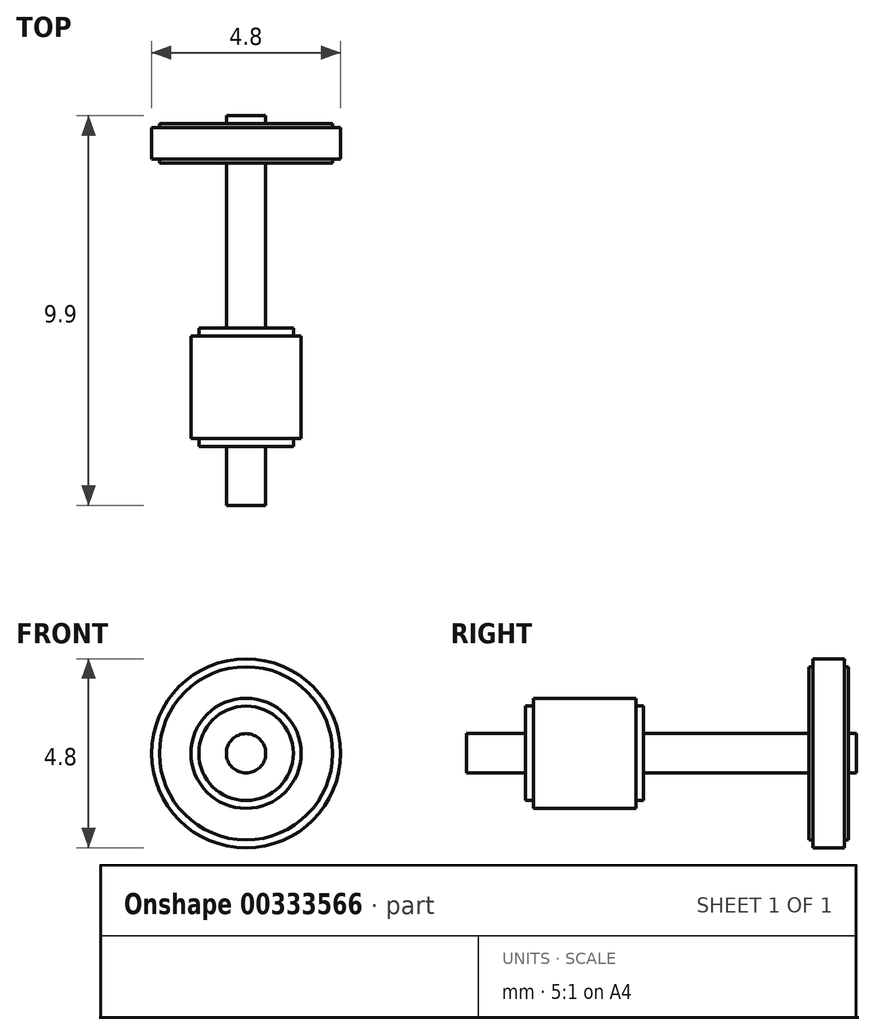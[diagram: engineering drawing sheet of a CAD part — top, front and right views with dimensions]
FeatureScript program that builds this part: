
annotation { "Feature Type Name" : "Feature", "Feature Type Description" : "" }
export const myFeature = defineFeature(function(context is Context, id is Id, definition is map)
    precondition{}
    {
        {
            var Q0;
            Q0=qCreatedBy(makeId("Right.planeOp"),FACE);
            var sketch = newSketch(context, id + "F0", { "sketchPlane" : qUnion([Q0])});
            skLineSegment(sketch, "E0", {"start": v(-1.5, 0) * mm, "end": v(-1.5, 0.5) * mm});
            skLineSegment(sketch, "E1", {"start": v(-1.5, 0.5) * mm, "end": v(0, 0.5) * mm});
            skLineSegment(sketch, "E2", {"start": v(0, 0.5) * mm, "end": v(0, 1.4) * mm});
            skLineSegment(sketch, "E3", {"start": v(0, 1.4) * mm, "end": v(3, 1.4) * mm});
            skLineSegment(sketch, "E4", {"start": v(3, 1.4) * mm, "end": v(3, 0.5) * mm});
            skLineSegment(sketch, "E5", {"start": v(3, 0.5) * mm, "end": v(7.2, 0.5) * mm});
            skLineSegment(sketch, "E6", {"start": v(7.2, 0.5) * mm, "end": v(7.2, 2.4) * mm});
            skLineSegment(sketch, "E7", {"start": v(7.2, 2.4) * mm, "end": v(8.2, 2.4) * mm});
            skLineSegment(sketch, "E8", {"start": v(8.2, 2.4) * mm, "end": v(8.2, 0.5) * mm});
            skLineSegment(sketch, "E9", {"start": v(8.2, 0.5) * mm, "end": v(8.4, 0.5) * mm});
            skLineSegment(sketch, "E10", {"start": v(8.4, 0.5) * mm, "end": v(8.4, 0) * mm});
            skLineSegment(sketch, "E11", {"start": v(8.4, 0) * mm, "end": v(-1.5, 0) * mm});
            skSolve(sketch);
        }
        {
            var Q0;
            Q0=qSketchRegion(id+"F0",true);
            var Q1;
            Q1=sQuery(id+"F0.wireOp",EDGE,"E11");
            revolve(context, id + "F1", {"entities" : qUnion([Q0]), "axis" : qUnion([Q1]), "revolveType" : RevolveType.FULL});
        }
        {
            var Q0;
            Q0=qCreatedBy(makeId("Right.planeOp"),FACE);
            var sketch = newSketch(context, id + "F2", { "sketchPlane" : qUnion([Q0])});
            skLineSegment(sketch, "E12.0", {"start": v(0, 1.4) * mm, "end": v(3, 1.4) * mm});
            skLineSegment(sketch, "E13.0", {"start": v(0, 0.5) * mm, "end": v(0, 1.4) * mm});
            skLineSegment(sketch, "E14.0", {"start": v(3, 1.4) * mm, "end": v(3, 0.5) * mm});
            skLineSegment(sketch, "E15.bottom", {"start": v(0, 1.4) * mm, "end": v(0.2, 1.4) * mm});
            skLineSegment(sketch, "E15.top", {"start": v(0, 1.2) * mm, "end": v(0.2, 1.2) * mm});
            skLineSegment(sketch, "E15.left", {"start": v(0, 1.4) * mm, "end": v(0, 1.2) * mm});
            skLineSegment(sketch, "E15.right", {"start": v(0.2, 1.4) * mm, "end": v(0.2, 1.2) * mm});
            skLineSegment(sketch, "E16.bottom", {"start": v(3, 1.4) * mm, "end": v(2.8, 1.4) * mm});
            skLineSegment(sketch, "E16.top", {"start": v(3, 1.2) * mm, "end": v(2.8, 1.2) * mm});
            skLineSegment(sketch, "E16.left", {"start": v(3, 1.4) * mm, "end": v(3, 1.2) * mm});
            skLineSegment(sketch, "E16.right", {"start": v(2.8, 1.4) * mm, "end": v(2.8, 1.2) * mm});
            skSolve(sketch);
        }
        {
            var Q0;
            Q0 = qSketchRegion(id + "F2", true);
            var Q1;
            Q1=sQuery(id+"F0.wireOp",EDGE,"E11");
            revolve(context, id + "F3", {"operationType" : NewBodyOperationType.REMOVE, "surfaceOperationType" : NewSurfaceOperationType.NEW, "entities" : qUnion([Q0]), "axis" : qUnion([Q1]), "revolveType" : RevolveType.FULL, "oppositeDirection" : true});
        }
        {
            var Q0;
            Q0=qCreatedBy(makeId("Right.planeOp"),FACE);
            var sketch = newSketch(context, id + "F4", { "sketchPlane" : qUnion([Q0])});
            skLineSegment(sketch, "E17.0", {"start": v(7.2, 2.4) * mm, "end": v(8.2, 2.4) * mm});
            skLineSegment(sketch, "E18", {"start": v(8.2, -2.4) * mm, "end": v(7.2, -2.4) * mm});
            skLineSegment(sketch, "E19.0", {"start": v(8.2, 2.4) * mm, "end": v(8.2, 0.5) * mm});
            skLineSegment(sketch, "E20.bottom", {"start": v(8.2, 2.4) * mm, "end": v(8.1, 2.4) * mm});
            skLineSegment(sketch, "E20.top", {"start": v(8.2, 2.2) * mm, "end": v(8.1, 2.2) * mm});
            skLineSegment(sketch, "E20.left", {"start": v(8.2, 2.4) * mm, "end": v(8.2, 2.2) * mm});
            skLineSegment(sketch, "E20.right", {"start": v(8.1, 2.4) * mm, "end": v(8.1, 2.2) * mm});
            skLineSegment(sketch, "E21.bottom", {"start": v(7.2, 2.4) * mm, "end": v(7.3, 2.4) * mm});
            skLineSegment(sketch, "E21.top", {"start": v(7.2, 2.2) * mm, "end": v(7.3, 2.2) * mm});
            skLineSegment(sketch, "E21.left", {"start": v(7.2, 2.4) * mm, "end": v(7.2, 2.2) * mm});
            skLineSegment(sketch, "E21.right", {"start": v(7.3, 2.4) * mm, "end": v(7.3, 2.2) * mm});
            skSolve(sketch);
        }
        {
            var Q0;
            Q0 = qSketchRegion(id + "F4", true);
            var Q1;
            Q1=sQuery(id+"F0.wireOp",EDGE,"E11");
            revolve(context, id + "F5", {"operationType" : NewBodyOperationType.REMOVE, "surfaceOperationType" : NewSurfaceOperationType.NEW, "entities" : qUnion([Q0]), "axis" : qUnion([Q1]), "revolveType" : RevolveType.FULL, "oppositeDirection" : true});
        }
    });
